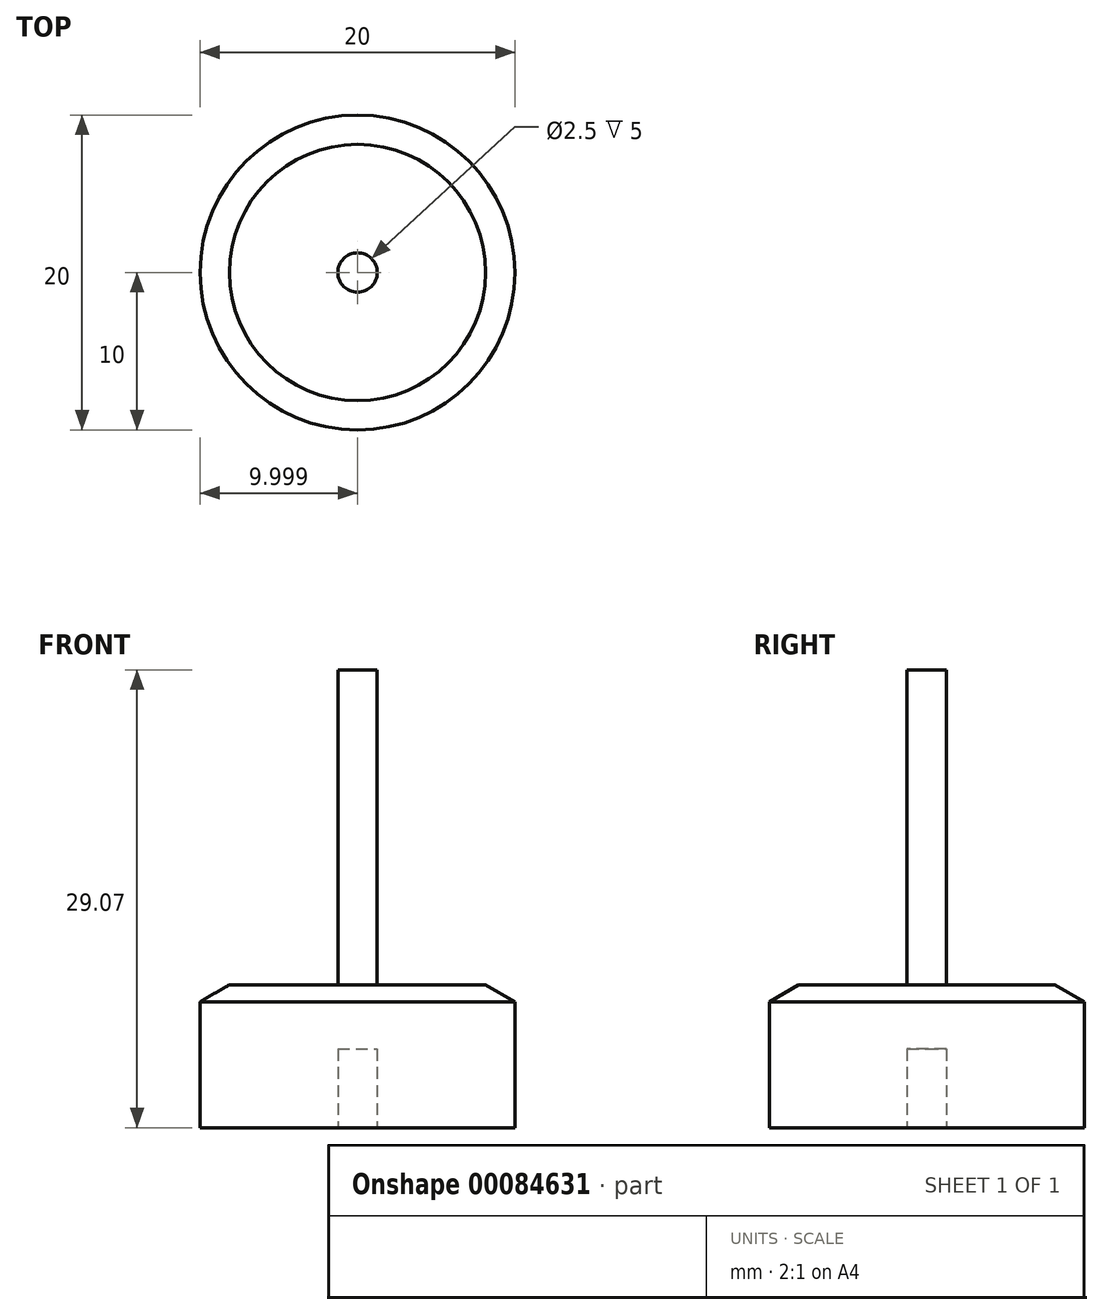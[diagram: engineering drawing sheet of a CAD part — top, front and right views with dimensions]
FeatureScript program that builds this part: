
annotation { "Feature Type Name" : "Feature", "Feature Type Description" : "" }
export const myFeature = defineFeature(function(context is Context, id is Id, definition is map)
    precondition{}
    {
        {
            var Q0;
            Q0=qCreatedBy(makeId("Front.planeOp"),FACE);
            var sketch = newSketch(context, id + "F0", { "sketchPlane" : qUnion([Q0])});
            skLineSegment(sketch, "E0.bottom", {"start": v(-30.55, 8) * mm, "end": v(-20.55, 8) * mm});
            skLineSegment(sketch, "E0.top", {"start": v(-30.55, 0) * mm, "end": v(-21.8, 0) * mm});
            skLineSegment(sketch, "E0.left", {"start": v(-30.55, 8) * mm, "end": v(-30.55, 0) * mm});
            skPoint(sketch, "E1", {"position": v(-20.55, 8) * mm});
            skPoint(sketch, "E2", {"position": v(-20.55, 0) * mm});
            skPoint(sketch, "E3", {"position": v(-20.55, 9.07) * mm});
            skLineSegment(sketch, "E4", {"start": v(-20.55, 8) * mm, "end": v(-20.55, 9.07) * mm});
            skLineSegment(sketch, "E5", {"start": v(-30.55, 8) * mm, "end": v(-28.7, 9.07) * mm});
            skLineSegment(sketch, "E6", {"start": v(-28.7, 9.07) * mm, "end": v(-20.55, 9.07) * mm});
            skLineSegment(sketch, "E7", {"start": v(-20.55, 8) * mm, "end": v(-20.55, 5) * mm});
            skPoint(sketch, "E0.right.end.orphan", {"position": v(-10.55, 0) * mm});
            skPoint(sketch, "E8.start.orphan", {"position": v(-10.55, 8) * mm});
            skLineSegment(sketch, "E9", {"start": v(-20.55, 9.07) * mm, "end": v(-20.55, 29.07) * mm});
            skLineSegment(sketch, "E10", {"start": v(-20.55, 29.07) * mm, "end": v(-21.8, 29.07) * mm});
            skLineSegment(sketch, "E11", {"start": v(-21.8, 29.07) * mm, "end": v(-21.8, 0) * mm});
            skPoint(sketch, "E12.start.orphan", {"position": v(-20.55, 4) * mm});
            skLineSegment(sketch, "E13", {"start": v(-20.55, 5) * mm, "end": v(-21.8, 5) * mm});
            skPoint(sketch, "E14", {"position": v(-20.55, 5) * mm});
            skSolve(sketch);
        }
        {
            var Q0;
            {var subQ0=sQuery(id+"F0.wireOp",EDGE,"E9");Q0=makeQuery(id+"F0.imprint","IMPRINT",FACE,{"disambiguationData":[TD([[makeQuery(id+"F0.imprint","IMPRINT",EDGE,{"derivedFrom":subQ0}),1.0]])]});}
            var Q1;
            {var subQ5=sQuery(id+"F0.wireOp",EDGE,"E0.top");Q1=makeQuery(id+"F0.imprint","IMPRINT",FACE,{"disambiguationData":[TD([[makeQuery(id+"F0.imprint","IMPRINT",EDGE,{"derivedFrom":subQ5}),1.0]])]});}
            var Q2;
            {var subQ0=sQuery(id+"F0.wireOp",EDGE,"E5");Q2=makeQuery(id+"F0.imprint","IMPRINT",FACE,{"disambiguationData":[TD([[makeQuery(id+"F0.imprint","IMPRINT",EDGE,{"derivedFrom":subQ0}),-1.0]])]});}
            var Q3;
            {var subQ0=sQuery(id+"F0.wireOp",EDGE,"E7");Q3=makeQuery(id+"F0.imprint","IMPRINT",FACE,{"disambiguationData":[TD([[makeQuery(id+"F0.imprint","IMPRINT",EDGE,{"derivedFrom":subQ0}),-1.0]])]});}
            var Q4;
            {var subQ0=sQuery(id+"F0.wireOp",EDGE,"E4");Q4=makeQuery(id+"F0.imprint","IMPRINT",FACE,{"disambiguationData":[TD([[makeQuery(id+"F0.imprint","IMPRINT",EDGE,{"derivedFrom":subQ0}),1.0]])]});}
            var Q5;
            Q5=sQuery(id+"F0.wireOp",EDGE,"E9");
            revolve(context, id + "F1", {"entities" : qUnion([Q0, Q1, Q2, Q3, Q4]), "axis" : qUnion([Q5]), "revolveType" : RevolveType.FULL});
        }
    });
